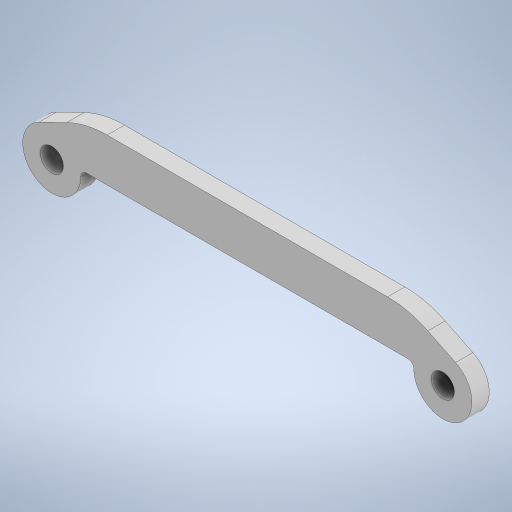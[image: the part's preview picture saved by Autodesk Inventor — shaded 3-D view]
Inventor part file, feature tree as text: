
AUTODESK INVENTOR PART (.ipt)
format: ipt  version: 2024 (Build 280153000, 153)  size: 265,216 bytes
history: native  units: in
note: dims shown in document units (in); Inventor stores cm internally (conversion verified against a paired STEP export)
features: fillet x2, extrude x1, direct_edit x1, sketch x1, other x1
ambient origin geometry x8: Origin, YZ Plane, XZ Plane, XY Plane, X Axis, Y Axis, Z Axis, Center Point
bodies: Solid1 (feature_tree)
feature tree (6):
  extrude  "Extrusion1"  Depth=0.3937in
  fillet  "Fillet1"  Radius=0.125in
  fillet  "Fillet2"  Radius=0.188in
  direct_edit  "Direct Edit1"
  sketch  "Sketch1"  dims[d0=1.75in d1=0.1575in d2=0.125in d3=0.188in d4=0.25in d5=1.06in d6=0.0938in d7=0.0in d8=0.5in d9=0.032in d10=3.937in d11=0.3937in d12=0.3937in]
  other  "Scale1"
